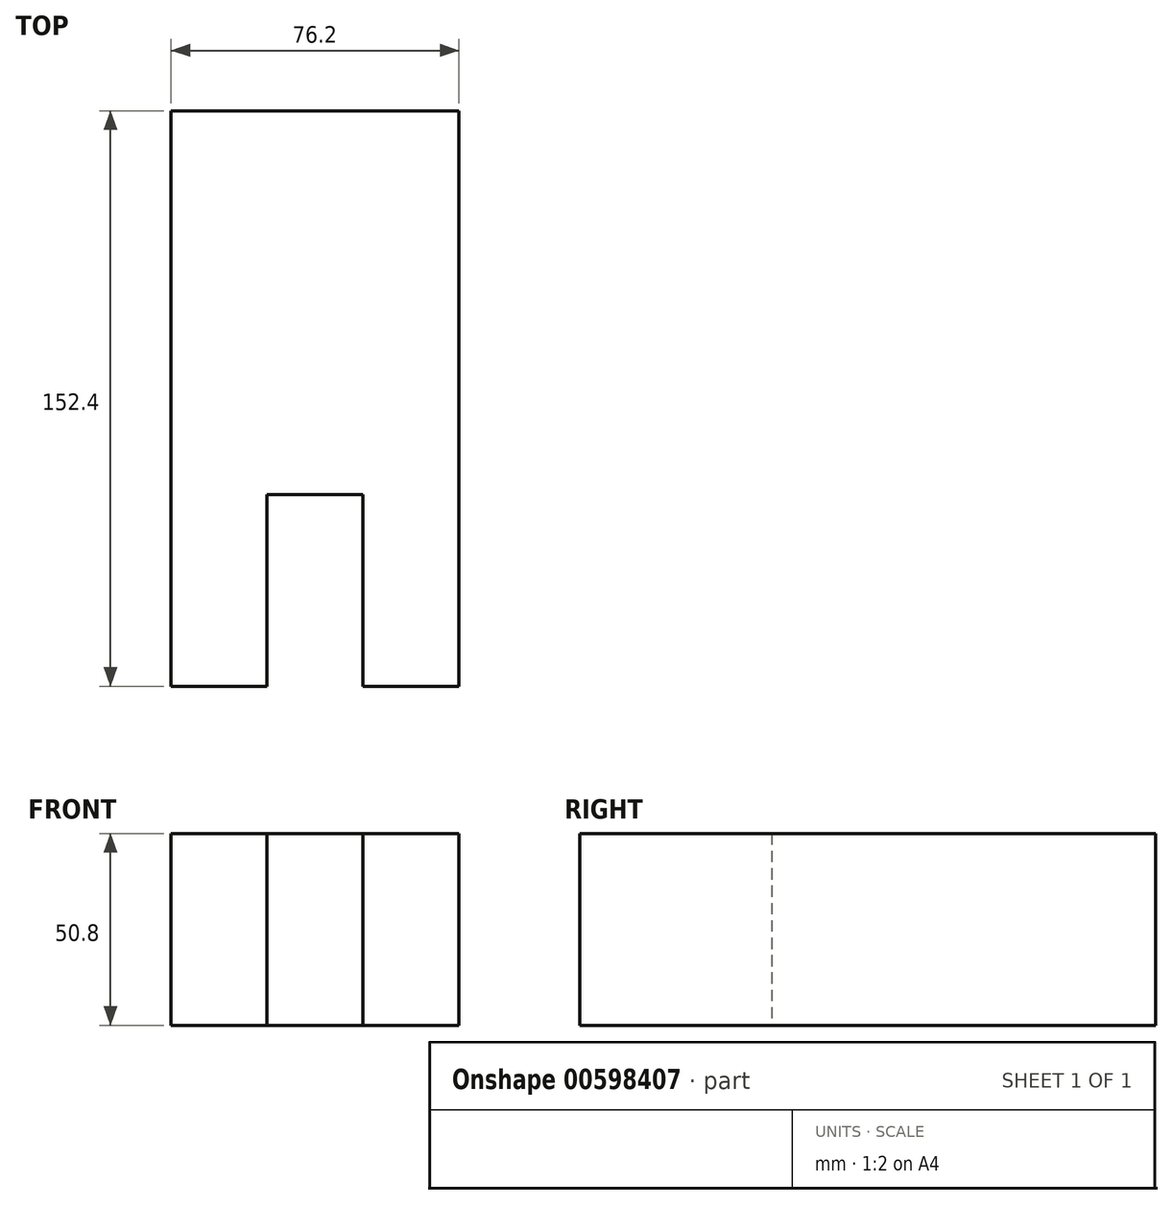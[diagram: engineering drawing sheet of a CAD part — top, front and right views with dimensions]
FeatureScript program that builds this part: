
annotation { "Feature Type Name" : "Feature", "Feature Type Description" : "" }
export const myFeature = defineFeature(function(context is Context, id is Id, definition is map)
    precondition{}
    {
        {
            var Q0;
            Q0=qCreatedBy(makeId("Top.planeOp"),FACE);
            var sketch = newSketch(context, id + "F0", { "sketchPlane" : qUnion([Q0])});
            skLineSegment(sketch, "E0", {"start": v(-37.67, 122.13) * mm, "end": v(38.53, 122.13) * mm});
            skLineSegment(sketch, "E1", {"start": v(-37.67, 122.13) * mm, "end": v(-37.67, -30.27) * mm});
            skLineSegment(sketch, "E2", {"start": v(-37.67, -30.27) * mm, "end": v(-12.27, -30.27) * mm});
            skLineSegment(sketch, "E3", {"start": v(-12.27, -30.27) * mm, "end": v(-12.27, 20.53) * mm});
            skLineSegment(sketch, "E4", {"start": v(-12.27, 20.53) * mm, "end": v(13.13, 20.53) * mm});
            skLineSegment(sketch, "E5", {"start": v(13.13, 20.53) * mm, "end": v(13.13, -30.27) * mm});
            skLineSegment(sketch, "E6", {"start": v(13.13, -30.27) * mm, "end": v(38.53, -30.27) * mm});
            skLineSegment(sketch, "E7", {"start": v(38.53, -30.27) * mm, "end": v(38.53, 122.13) * mm});
            skSolve(sketch);
        }
        {
            var Q0;
            Q0 = qSketchRegion(id + "F0", true);
            extrude(context, id + "F1", {"entities" : qUnion([Q0]), "depth" : 50.8 * mm, "offsetDistance" : 25.4 * mm});
        }
    });
